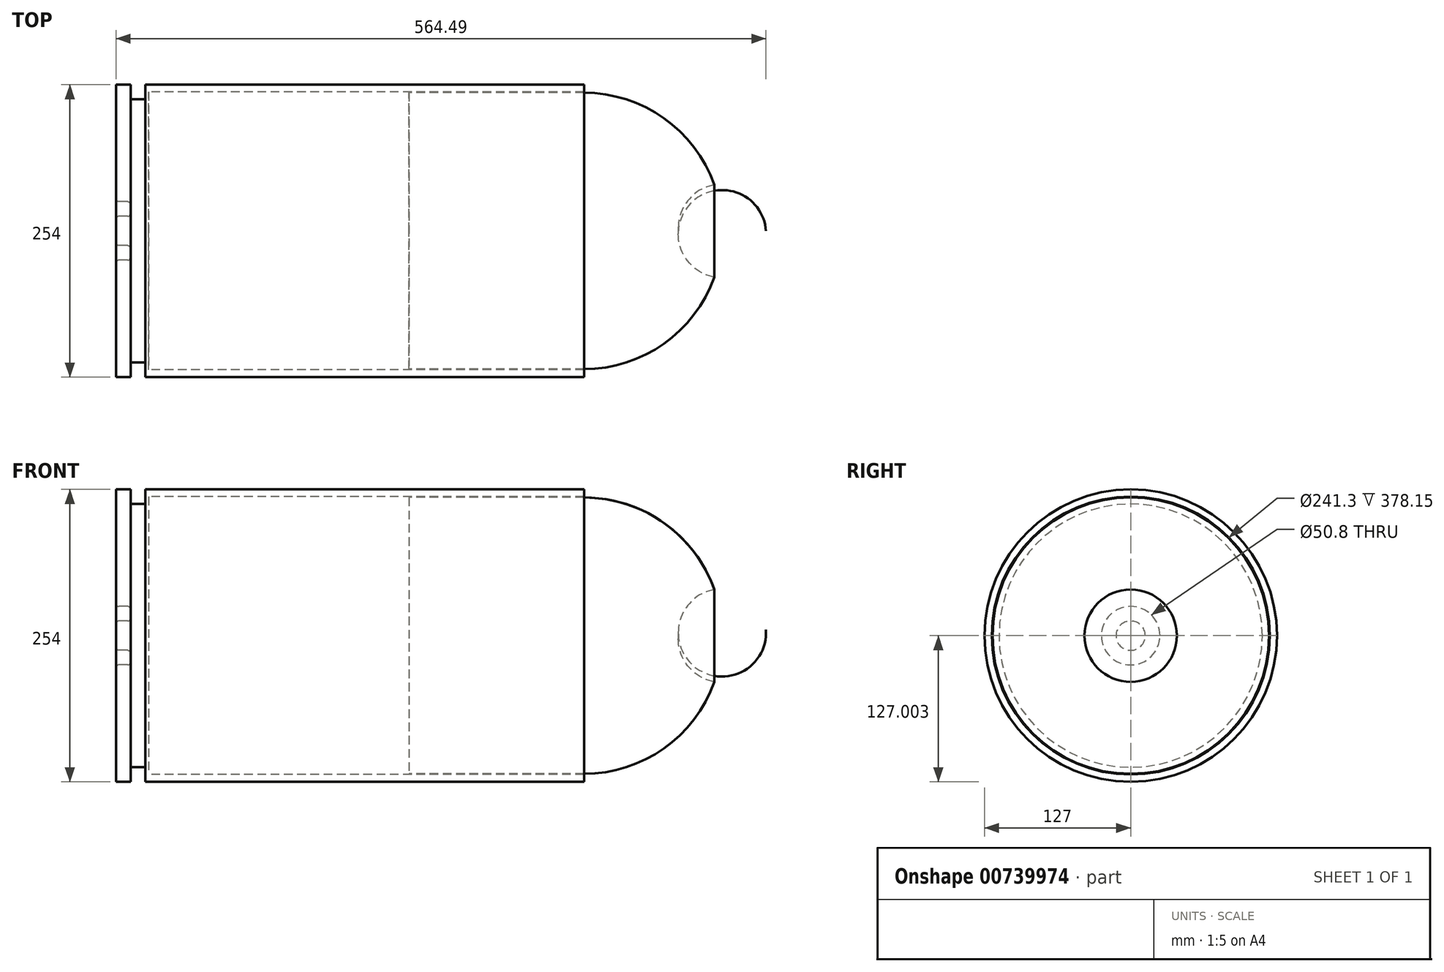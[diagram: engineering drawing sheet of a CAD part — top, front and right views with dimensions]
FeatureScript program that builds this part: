
annotation { "Feature Type Name" : "Feature", "Feature Type Description" : "" }
export const myFeature = defineFeature(function(context is Context, id is Id, definition is map)
    precondition{}
    {
        {
            var Q0;
            Q0=qCreatedBy(makeId("Front.planeOp"),FACE);
            var sketch = newSketch(context, id + "F0", { "sketchPlane" : qUnion([Q0])});
            skLineSegment(sketch, "E0", {"start": v(-64.55, 38.7) * mm, "end": v(-51.85, 38.7) * mm});
            skLineSegment(sketch, "E1", {"start": v(-51.85, 38.7) * mm, "end": v(-51.85, 26) * mm});
            skLineSegment(sketch, "E2", {"start": v(-51.85, 26) * mm, "end": v(-39.15, 26) * mm});
            skLineSegment(sketch, "E3", {"start": v(-39.15, 26) * mm, "end": v(-39.15, 38.7) * mm});
            skLineSegment(sketch, "E4", {"start": v(-39.15, 38.7) * mm, "end": v(341.85, 38.7) * mm});
            skLineSegment(sketch, "E5", {"start": v(-64.55, -88.3) * mm, "end": v(-64.55, -78.15) * mm});
            skLineSegment(sketch, "E6", {"start": v(-62.01, -75.6) * mm, "end": v(-54.4, -75.6) * mm});
            skLineSegment(sketch, "E7", {"start": v(-51.85, -73.07) * mm, "end": v(-51.85, -65.45) * mm});
            skLineSegment(sketch, "E8", {"start": v(-54.4, -62.9) * mm, "end": v(-62.01, -62.9) * mm});
            skLineSegment(sketch, "E9", {"start": v(-64.55, -60.37) * mm, "end": v(-64.55, 38.7) * mm});
            skPoint(sketch, "E10.visualSharp", {"position": v(-64.55, -75.6) * mm});
            skArc(sketch, "E10.filletArc", {"start": v(-62.01, -75.6) * mm, "mid": v(-63.8, -76.35) * mm, "end": v(-64.55, -78.15) * mm});
            skPoint(sketch, "E11.visualSharp", {"position": v(-51.85, -75.6) * mm});
            skArc(sketch, "E11.filletArc", {"start": v(-54.4, -75.6) * mm, "mid": v(-52.6, -74.86) * mm, "end": v(-51.85, -73.07) * mm});
            skPoint(sketch, "E12.visualSharp", {"position": v(-51.85, -62.9) * mm});
            skArc(sketch, "E12.filletArc", {"start": v(-51.85, -65.45) * mm, "mid": v(-52.6, -63.65) * mm, "end": v(-54.4, -62.9) * mm});
            skPoint(sketch, "E13.visualSharp", {"position": v(-64.55, -62.9) * mm});
            skArc(sketch, "E13.filletArc", {"start": v(-64.55, -60.37) * mm, "mid": v(-63.8, -62.16) * mm, "end": v(-62.01, -62.9) * mm});
            skLineSegment(sketch, "E14", {"start": v(341.85, 38.7) * mm, "end": v(341.85, 32.34) * mm});
            skLineSegment(sketch, "E15", {"start": v(189.45, 32.34) * mm, "end": v(341.85, 32.34) * mm});
            skLineSegment(sketch, "E16", {"start": v(-64.55, -88.3) * mm, "end": v(189.45, -88.3) * mm});
            skLineSegment(sketch, "E17", {"start": v(189.45, -88.3) * mm, "end": v(189.45, 32.34) * mm});
            skLineSegment(sketch, "E18", {"start": v(341.85, 32.34) * mm, "end": v(341.85, 31.7) * mm});
            skLineSegment(sketch, "E19", {"start": v(341.85, 31.7) * mm, "end": v(190.08, 31.7) * mm});
            skLineSegment(sketch, "E20.0", {"start": v(190.08, -88.3) * mm, "end": v(190.08, 31.7) * mm});
            skLineSegment(sketch, "E21.bottom", {"start": v(190.08, -88.3) * mm, "end": v(341.85, -88.3) * mm});
            skLineSegment(sketch, "E21.top", {"start": v(190.08, 31.7) * mm, "end": v(341.85, 31.7) * mm});
            skLineSegment(sketch, "E22", {"start": v(189.45, -88.3) * mm, "end": v(190.08, -88.3) * mm});
            skArc(sketch, "E23", {"start": v(454.98, -48.23) * mm, "mid": v(411.11, 9.7) * mm, "end": v(341.85, 31.7) * mm});
            skLineSegment(sketch, "E24", {"start": v(341.85, -88.3) * mm, "end": v(423.82, -88.3) * mm});
            skPoint(sketch, "E25.visualSharp", {"position": v(461.86, -88.3) * mm});
            skArc(sketch, "E25.filletArc", {"start": v(459.3, -88.3) * mm, "mid": v(461.11, -87.54) * mm, "end": v(461.84, -85.71) * mm});
            skArc(sketch, "E26", {"start": v(454.98, -48.23) * mm, "mid": v(431.76, -62.33) * mm, "end": v(423.82, -88.3) * mm});
            skLineSegment(sketch, "E27.bottom", {"start": v(189.45, 32.34) * mm, "end": v(-36.3, 32.34) * mm});
            skLineSegment(sketch, "E27.left", {"start": v(189.45, 32.34) * mm, "end": v(189.45, -88.3) * mm});
            skLineSegment(sketch, "E27.right", {"start": v(-36.3, 32.34) * mm, "end": v(-36.3, -88.3) * mm});
            skSolve(sketch);
        }
        {
            var Q0;
            Q0=makeQuery(id+"F0.imprint","IMPRINT",FACE,{"disambiguationData":[TD([[makeQuery(id+"F0.imprint","IMPRINT",EDGE,{"derivedFrom":sQuery(id+"F0.wireOp",EDGE,"E0")}),-1.0]])]});
            var Q1;
            Q1=sQuery(id+"F0.wireOp",EDGE,"E16");
            revolve(context, id + "F1", {"surfaceOperationType" : NewSurfaceOperationType.NEW, "entities" : qUnion([Q0]), "axis" : qUnion([Q1]), "revolveType" : RevolveType.FULL});
        }
        {
            var Q0;
            Q0=makeQuery(id+"F0.imprint","IMPRINT",FACE,{"disambiguationData":[TD([[makeQuery(id+"F0.imprint","IMPRINT",EDGE,{"derivedFrom":sQuery(id+"F0.wireOp",EDGE,"E21.bottom")}),1.0]])]});
            var Q1;
            Q1=sQuery(id+"F0.wireOp",EDGE,"E24");
            revolve(context, id + "F2", {"surfaceOperationType" : NewSurfaceOperationType.NEW, "entities" : qUnion([Q0]), "axis" : qUnion([Q1]), "revolveType" : RevolveType.FULL});
        }
    });
